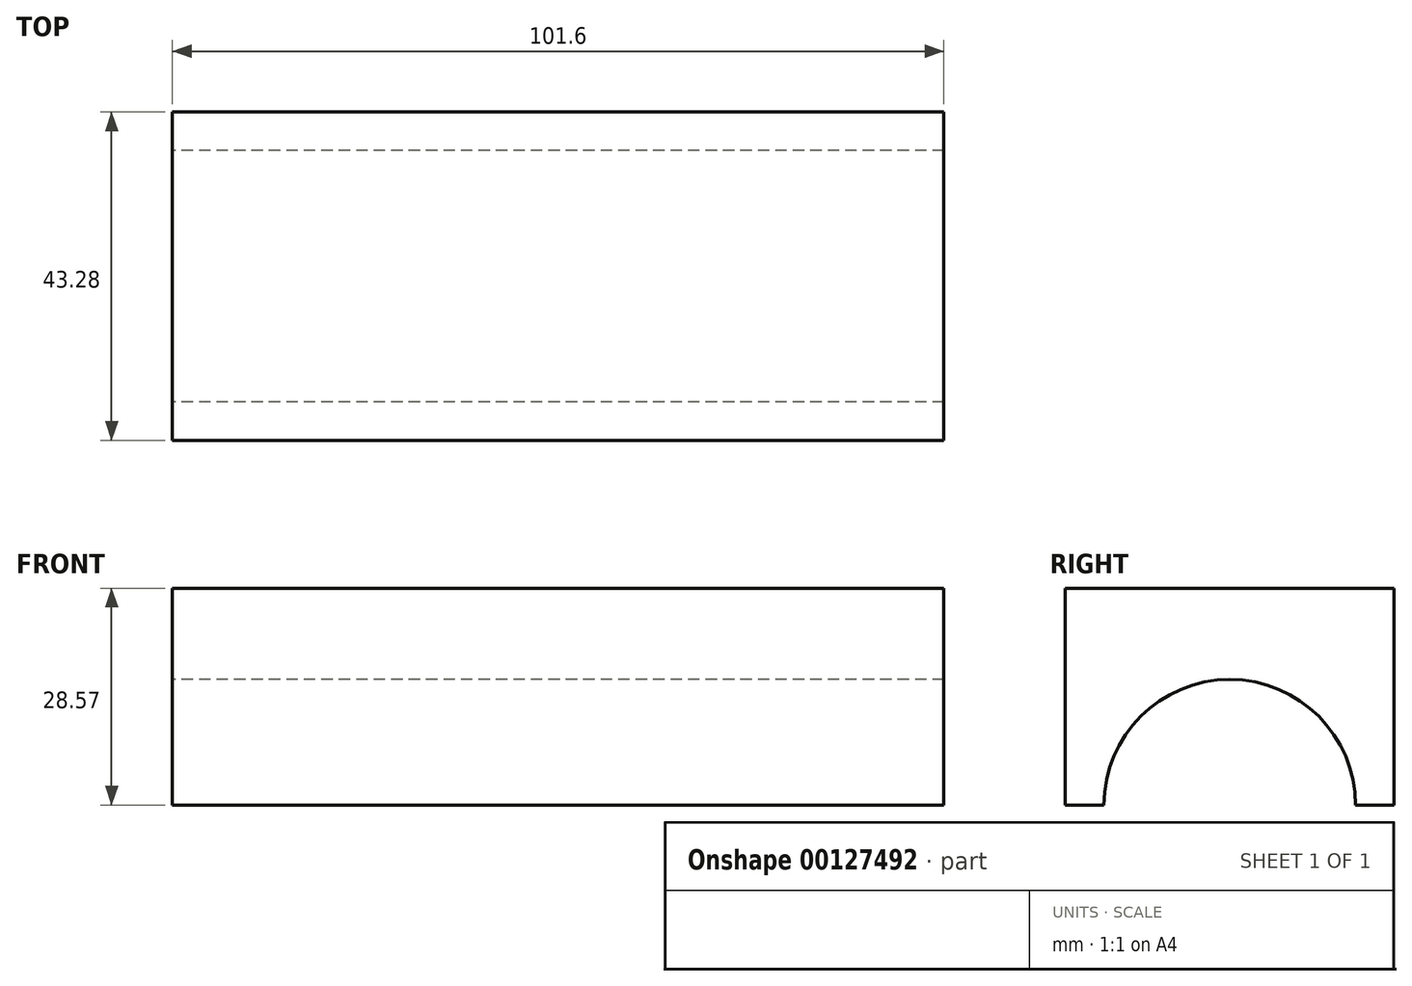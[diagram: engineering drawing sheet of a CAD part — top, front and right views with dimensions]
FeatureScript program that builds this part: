
annotation { "Feature Type Name" : "Feature", "Feature Type Description" : "" }
export const myFeature = defineFeature(function(context is Context, id is Id, definition is map)
    precondition{}
    {
        {
            var Q0;
            Q0=qCreatedBy(makeId("Right.planeOp"),FACE);
            var sketch = newSketch(context, id + "F0", { "sketchPlane" : qUnion([Q0])});
            skArc(sketch, "E0.0", {"start": v(16.56, -11.28) * mm, "mid": v(0, 5.28) * mm, "end": v(-16.56, -11.28) * mm});
            skLineSegment(sketch, "E1", {"start": v(-16.56, -11.28) * mm, "end": v(-21.64, -11.28) * mm});
            skLineSegment(sketch, "E2", {"start": v(16.56, -11.28) * mm, "end": v(21.64, -11.28) * mm});
            skLineSegment(sketch, "E3", {"start": v(-21.64, -11.28) * mm, "end": v(-21.64, 17.3) * mm});
            skLineSegment(sketch, "E4", {"start": v(21.64, -11.28) * mm, "end": v(21.64, 17.3) * mm});
            skLineSegment(sketch, "E5", {"start": v(-21.64, 17.3) * mm, "end": v(21.64, 17.3) * mm});
            skSolve(sketch);
        }
        {
            var Q0;
            Q0 = qSketchRegion(id + "F0", true);
            var Q1;
            Q1=sQuery(id+"F0.wireOp",EDGE,"E0.0");
            var Q2;
            Q2=sQuery(id+"F0.wireOp",EDGE,"E1");
            var Q3;
            Q3=sQuery(id+"F0.wireOp",EDGE,"E2");
            var Q4;
            Q4=sQuery(id+"F0.wireOp",EDGE,"E3");
            var Q5;
            Q5=sQuery(id+"F0.wireOp",EDGE,"E4");
            var Q6;
            Q6=sQuery(id+"F0.wireOp",EDGE,"E5");
            extrude(context, id + "F1", {"entities" : qUnion([Q0]), "surfaceEntities" : qUnion([Q1, Q2, Q3, Q4, Q5, Q6]), "depth" : 101.6 * mm});
        }
    });
